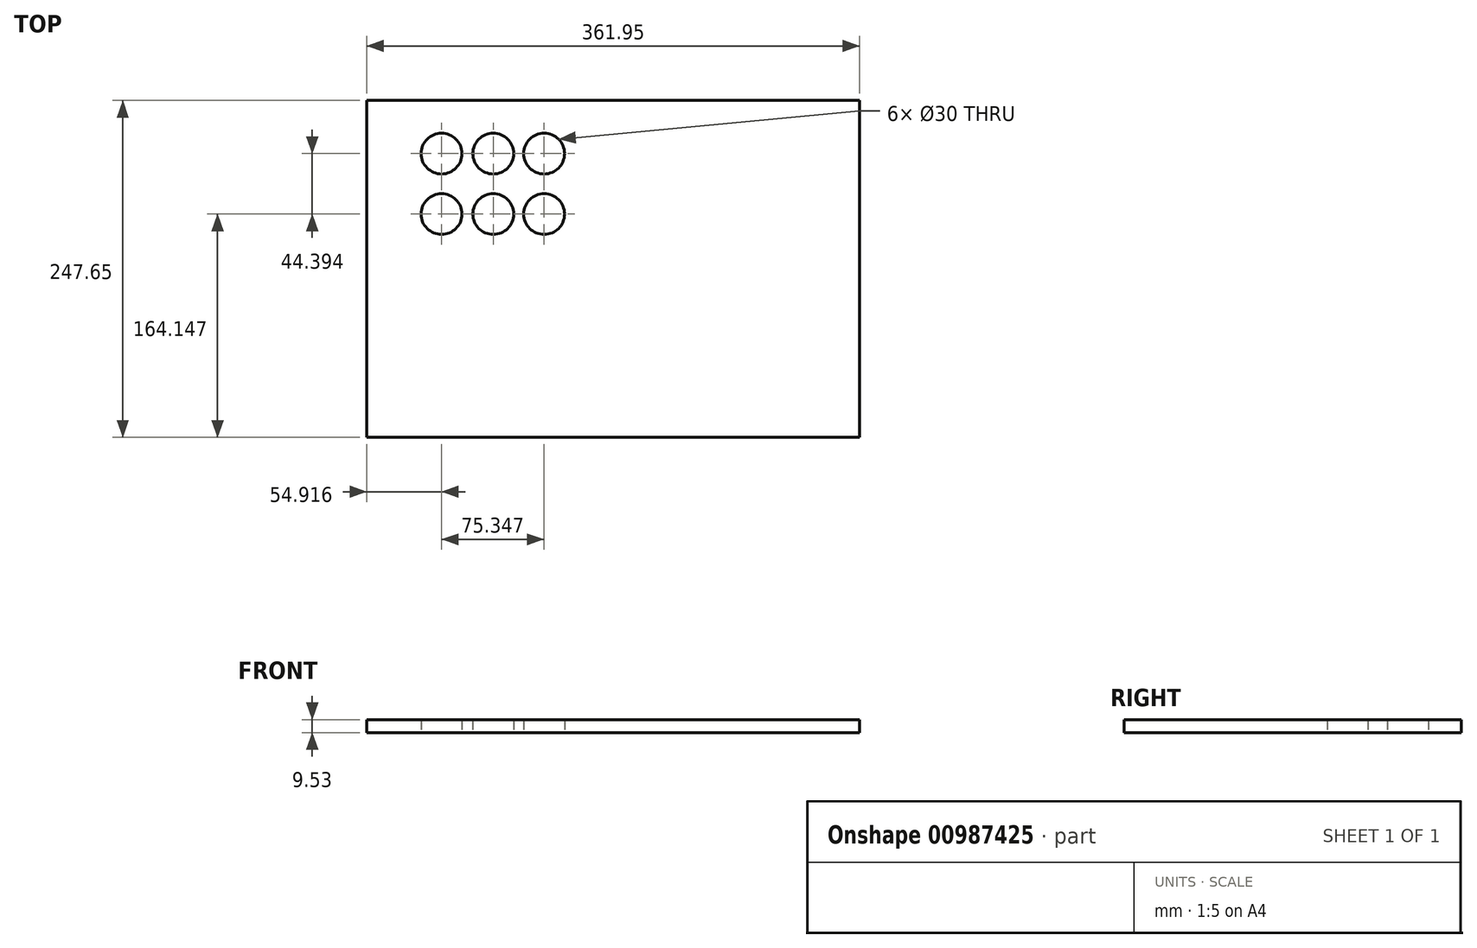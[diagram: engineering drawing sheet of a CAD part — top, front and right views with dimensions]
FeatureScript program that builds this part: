
annotation { "Feature Type Name" : "Feature", "Feature Type Description" : "" }
export const myFeature = defineFeature(function(context is Context, id is Id, definition is map)
    precondition{}
    {
        {
            var Q0;
            Q0=qCreatedBy(makeId("Top.planeOp"),FACE);
            var sketch = newSketch(context, id + "F0", { "sketchPlane" : qUnion([Q0])});
            skLineSegment(sketch, "E0.bottom", {"start": v(-329.03, 195.19) * mm, "end": v(32.92, 195.19) * mm});
            skLineSegment(sketch, "E0.top", {"start": v(-329.03, -52.46) * mm, "end": v(32.92, -52.46) * mm});
            skLineSegment(sketch, "E0.left", {"start": v(-329.03, 195.19) * mm, "end": v(-329.03, -52.46) * mm});
            skLineSegment(sketch, "E0.right", {"start": v(32.92, 195.19) * mm, "end": v(32.92, -52.46) * mm});
            skSolve(sketch);
        }
        {
            var Q0;
            Q0=makeQuery(id+"F0.imprint","IMPRINT",FACE,{"disambiguationData":[TD([[makeQuery(id+"F0.imprint","IMPRINT",EDGE,{"derivedFrom":sQuery(id+"F0.wireOp",EDGE,"E0.bottom")}),-1.0]])]});
            var Q1;
            Q1 = qSketchRegion(id + "F2", true);
            extrude(context, id + "F1", {"entities" : qUnion([Q0, Q1]), "oppositeDirection" : true, "depth" : 9.52 * mm, "offsetDistance" : 25.4 * mm});
        }
        {
            var Q0;
            Q0=makeQuery(id+"F1.opExtrude","CAP_FACE",FACE,{"disambiguationData":[OSD([sQuery(id+"F0.wireOp",EDGE,"E0.bottom"),sQuery(id+"F0.wireOp",EDGE,"E0.top"),sQuery(id+"F0.wireOp",EDGE,"E0.left"),sQuery(id+"F0.wireOp",EDGE,"E0.right")])],"isStart":false});
            var sketch = newSketch(context, id + "F2", { "sketchPlane" : qUnion([Q0])});
            skPoint(sketch, "E1", {"position": v(-274.11, -156.08) * mm});
            skPoint(sketch, "E2", {"position": v(-236.13, -156.08) * mm});
            skPoint(sketch, "E3", {"position": v(-198.77, -156.08) * mm});
            skPoint(sketch, "E4", {"position": v(-198.77, -111.69) * mm});
            skPoint(sketch, "E5", {"position": v(-236.13, -111.69) * mm});
            skPoint(sketch, "E6", {"position": v(-274.11, -111.69) * mm});
            skSolve(sketch);
        }
        {
            var Q0;
            Q0=sQuery(id+"F2.wireOp",VERTEX,"E5");
            var Q1;
            Q1=sQuery(id+"F2.wireOp",VERTEX,"E2");
            var Q2;
            Q2=sQuery(id+"F2.wireOp",VERTEX,"E4");
            var Q3;
            Q3=sQuery(id+"F2.wireOp",VERTEX,"E1");
            var Q4;
            Q4=sQuery(id+"F2.wireOp",VERTEX,"E3");
            var Q5;
            Q5=sQuery(id+"F2.wireOp",VERTEX,"E6");
            var Q6;
            Q6=makeQuery(id+"F1.opExtrude","SWEPT_BODY",BODY,{"disambiguationData":[OSD([sQuery(id+"F0.wireOp",EDGE,"E0.bottom"),sQuery(id+"F0.wireOp",EDGE,"E0.top"),sQuery(id+"F0.wireOp",EDGE,"E0.left"),sQuery(id+"F0.wireOp",EDGE,"E0.right")])]});
            hole(context, id + "F3", {"style" : HoleStyle.SIMPLE, "endStyle" : HoleEndStyle.THROUGH, "holeDiameter" : 30 * mm, "majorDiameter" : 6.35 * mm, "isTappedThrough" : true, "tappedDepth" : 12.7 * mm, "tapClearance" : 3, "locations" : qUnion([Q0, Q1, Q2, Q3, Q4, Q5]), "scope" : qUnion([Q6])});
        }
    });
